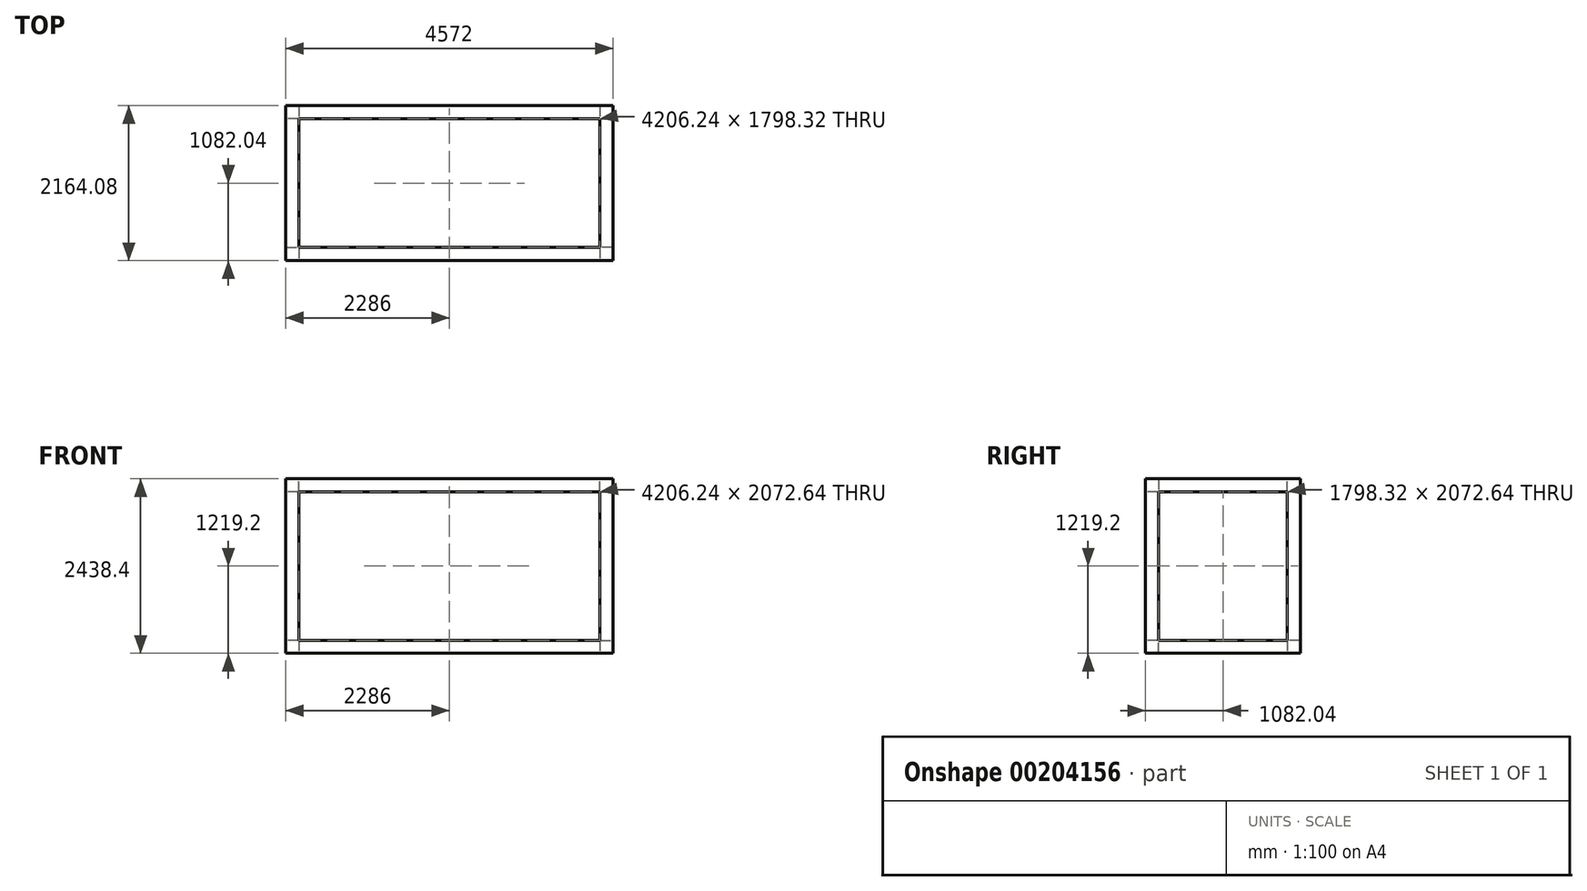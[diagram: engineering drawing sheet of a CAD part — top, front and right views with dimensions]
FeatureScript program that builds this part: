
annotation { "Feature Type Name" : "Feature", "Feature Type Description" : "" }
export const myFeature = defineFeature(function(context is Context, id is Id, definition is map)
    precondition{}
    {
        {
            var Q0;
            Q0=qCreatedBy(makeId("Front.planeOp"),FACE);
            var sketch = newSketch(context, id + "F0", { "sketchPlane" : qUnion([Q0])});
            skLineSegment(sketch, "E0.bottom", {"start": v(0, 0) * mm, "end": v(4572, 0) * mm});
            skLineSegment(sketch, "E0.top", {"start": v(0, 2438.4) * mm, "end": v(4572, 2438.4) * mm});
            skLineSegment(sketch, "E0.left", {"start": v(0, 0) * mm, "end": v(0, 2438.4) * mm});
            skLineSegment(sketch, "E0.right", {"start": v(4572, 0) * mm, "end": v(4572, 2438.4) * mm});
            skSolve(sketch);
        }
        {
            var Q0;
            Q0=makeQuery(id+"F0.imprint","IMPRINT",FACE,{"disambiguationData":[TD([[makeQuery(id+"F0.imprint","IMPRINT",EDGE,{"derivedFrom":sQuery(id+"F0.wireOp",EDGE,"E0.bottom")}),1.0]])]});
            extrude(context, id + "F1", {"entities" : qUnion([Q0]), "depth" : 182.88 * mm});
        }
        {
            var Q0;
            Q0=makeQuery(id+"F0.imprint","IMPRINT",FACE,{"disambiguationData":[TD([[makeQuery(id+"F0.imprint","IMPRINT",EDGE,{"derivedFrom":sQuery(id+"F0.wireOp",EDGE,"E0.bottom")}),1.0]])]});
            var sketch = newSketch(context, id + "F2", { "sketchPlane" : qUnion([Q0])});
            skLineSegment(sketch, "E1.bottom", {"start": v(0, 2438.4) * mm, "end": v(182.88, 2438.4) * mm});
            skLineSegment(sketch, "E1.top", {"start": v(0, 2255.52) * mm, "end": v(182.88, 2255.52) * mm});
            skLineSegment(sketch, "E1.left", {"start": v(0, 2438.4) * mm, "end": v(0, 2255.52) * mm});
            skLineSegment(sketch, "E1.right", {"start": v(182.88, 2438.4) * mm, "end": v(182.88, 2255.52) * mm});
            skLineSegment(sketch, "E2.bottom", {"start": v(0, 0) * mm, "end": v(182.88, 0) * mm});
            skLineSegment(sketch, "E2.top", {"start": v(0, 182.88) * mm, "end": v(182.88, 182.88) * mm});
            skLineSegment(sketch, "E2.left", {"start": v(0, 0) * mm, "end": v(0, 182.88) * mm});
            skLineSegment(sketch, "E2.right", {"start": v(182.88, 0) * mm, "end": v(182.88, 182.88) * mm});
            skLineSegment(sketch, "E3.bottom", {"start": v(4572, 0) * mm, "end": v(4389.12, 0) * mm});
            skLineSegment(sketch, "E3.top", {"start": v(4572, 182.88) * mm, "end": v(4389.12, 182.88) * mm});
            skLineSegment(sketch, "E3.left", {"start": v(4572, 0) * mm, "end": v(4572, 182.88) * mm});
            skLineSegment(sketch, "E3.right", {"start": v(4389.12, 0) * mm, "end": v(4389.12, 182.88) * mm});
            skLineSegment(sketch, "E4.bottom", {"start": v(4572, 2438.4) * mm, "end": v(4389.12, 2438.4) * mm});
            skLineSegment(sketch, "E4.top", {"start": v(4572, 2255.52) * mm, "end": v(4389.12, 2255.52) * mm});
            skLineSegment(sketch, "E4.left", {"start": v(4572, 2438.4) * mm, "end": v(4572, 2255.52) * mm});
            skLineSegment(sketch, "E4.right", {"start": v(4389.12, 2438.4) * mm, "end": v(4389.12, 2255.52) * mm});
            skSolve(sketch);
        }
        {
            var Q0;
            Q0 = qSketchRegion(id + "F2", true);
            extrude(context, id + "F3", {"entities" : qUnion([Q0]), "operationType" : NewBodyOperationType.ADD, "depth" : 1981.2 * mm});
        }
        {
            var Q0;
            Q0=makeQuery(id+"F3.opExtrude","CAP_FACE",FACE,{"disambiguationData":[OSD([sQuery(id+"F2.wireOp",EDGE,"E1.bottom"),sQuery(id+"F2.wireOp",EDGE,"E1.top"),sQuery(id+"F2.wireOp",EDGE,"E1.left"),sQuery(id+"F2.wireOp",EDGE,"E1.right")])],"isStart":false});
            var sketch = newSketch(context, id + "F4", { "sketchPlane" : qUnion([Q0])});
            skLineSegment(sketch, "E5.bottom", {"start": v(0, 2438.4) * mm, "end": v(4572, 2438.4) * mm});
            skLineSegment(sketch, "E5.top", {"start": v(0, 0) * mm, "end": v(4572, 0) * mm});
            skLineSegment(sketch, "E5.left", {"start": v(0, 2438.4) * mm, "end": v(0, 0) * mm});
            skLineSegment(sketch, "E5.right", {"start": v(4572, 2438.4) * mm, "end": v(4572, 0) * mm});
            skSolve(sketch);
        }
        {
            var Q0;
            {var subQ3=sQuery(id+"F4.wireOp",EDGE,"E5.top");Q0=makeQuery(id+"F4.imprint","IMPRINT",FACE,{"disambiguationData":[TD([[makeQuery(id+"F4.imprint","IMPRINT",EDGE,{"derivedFrom":subQ3}),1.0]])]});}
            var Q1;
            {var subQ4=makeQuery(id+"F3.opExtrude","CAP_EDGE",EDGE,{"disambiguationData":[OSD([sQuery(id+"F2.wireOp",EDGE,"E1.top")])],"isStart":false});Q1=makeQuery(id+"F4.imprint","IMPRINT",FACE,{"disambiguationData":[TD([[makeQuery(id+"F4.imprint","IMPRINT",EDGE,{"derivedFrom":subQ4}),1.0]])]});}
            extrude(context, id + "F5", {"entities" : qUnion([Q0, Q1]), "operationType" : NewBodyOperationType.ADD, "depth" : 182.88 * mm});
        }
        {
            var Q0;
            Q0=makeQuery(id+"F5.opExtrude","CAP_FACE",FACE,{"disambiguationData":[OSD([sQuery(id+"F4.wireOp",EDGE,"E5.bottom"),sQuery(id+"F4.wireOp",EDGE,"E5.top"),sQuery(id+"F4.wireOp",EDGE,"E5.left"),sQuery(id+"F4.wireOp",EDGE,"E5.right")])],"isStart":false});
            var sketch = newSketch(context, id + "F6", { "sketchPlane" : qUnion([Q0])});
            skLineSegment(sketch, "E6.bottom", {"start": v(0, 2438.4) * mm, "end": v(182.88, 2438.4) * mm});
            skLineSegment(sketch, "E6.top", {"start": v(0, 2255.52) * mm, "end": v(182.88, 2255.52) * mm});
            skLineSegment(sketch, "E6.left", {"start": v(0, 2438.4) * mm, "end": v(0, 2255.52) * mm});
            skLineSegment(sketch, "E6.right", {"start": v(182.88, 2438.4) * mm, "end": v(182.88, 2255.52) * mm});
            skLineSegment(sketch, "E7.bottom", {"start": v(0, 0) * mm, "end": v(182.88, 0) * mm});
            skLineSegment(sketch, "E7.top", {"start": v(0, 182.88) * mm, "end": v(182.88, 182.88) * mm});
            skLineSegment(sketch, "E7.left", {"start": v(0, 0) * mm, "end": v(0, 182.88) * mm});
            skLineSegment(sketch, "E7.right", {"start": v(182.88, 0) * mm, "end": v(182.88, 182.88) * mm});
            skLineSegment(sketch, "E8.bottom", {"start": v(4572, 0) * mm, "end": v(4389.12, 0) * mm});
            skLineSegment(sketch, "E8.top", {"start": v(4572, 182.88) * mm, "end": v(4389.12, 182.88) * mm});
            skLineSegment(sketch, "E8.left", {"start": v(4572, 0) * mm, "end": v(4572, 182.88) * mm});
            skLineSegment(sketch, "E8.right", {"start": v(4389.12, 0) * mm, "end": v(4389.12, 182.88) * mm});
            skLineSegment(sketch, "E9.bottom", {"start": v(4572, 2438.4) * mm, "end": v(4389.12, 2438.4) * mm});
            skLineSegment(sketch, "E9.top", {"start": v(4572, 2255.52) * mm, "end": v(4389.12, 2255.52) * mm});
            skLineSegment(sketch, "E9.left", {"start": v(4572, 2438.4) * mm, "end": v(4572, 2255.52) * mm});
            skLineSegment(sketch, "E10", {"start": v(4389.12, 2438.4) * mm, "end": v(4389.12, 2255.52) * mm});
            skLineSegment(sketch, "E11.bottom", {"start": v(182.88, 182.88) * mm, "end": v(4389.12, 182.88) * mm});
            skLineSegment(sketch, "E11.top", {"start": v(182.88, 2255.52) * mm, "end": v(4389.12, 2255.52) * mm});
            skLineSegment(sketch, "E11.left", {"start": v(182.88, 182.88) * mm, "end": v(182.88, 2255.52) * mm});
            skLineSegment(sketch, "E11.right", {"start": v(4389.12, 182.88) * mm, "end": v(4389.12, 2255.52) * mm});
            skSolve(sketch);
        }
        {
            var Q0;
            Q0=makeQuery(id+"F6.imprint","IMPRINT",FACE,{"disambiguationData":[TD([[makeQuery(id+"F6.imprint","IMPRINT",EDGE,{"derivedFrom":sQuery(id+"F6.wireOp",EDGE,"E11.bottom")}),1.0]])]});
            extrude(context, id + "F7", {"entities" : qUnion([Q0]), "operationType" : NewBodyOperationType.REMOVE, "oppositeDirection" : true, "depth" : 2286 * mm});
        }
    });
